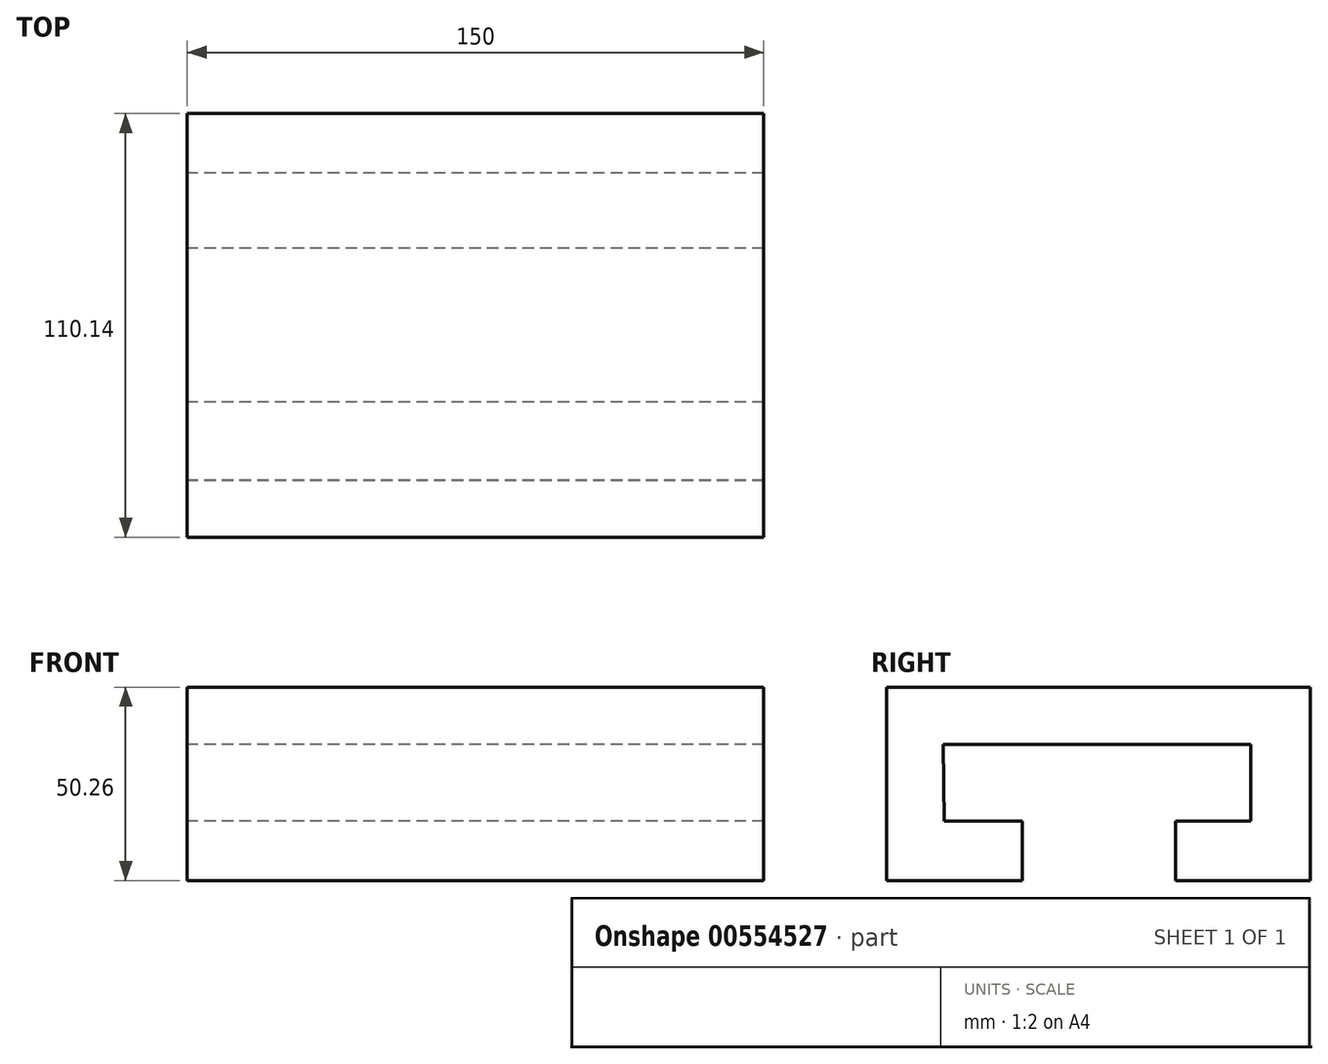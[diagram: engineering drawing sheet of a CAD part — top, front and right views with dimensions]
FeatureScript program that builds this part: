
annotation { "Feature Type Name" : "Feature", "Feature Type Description" : "" }
export const myFeature = defineFeature(function(context is Context, id is Id, definition is map)
    precondition{}
    {
        {
            var Q0;
            Q0=qCreatedBy(makeId("Right.planeOp"),FACE);
            var sketch = newSketch(context, id + "F0", { "sketchPlane" : qUnion([Q0])});
            skLineSegment(sketch, "E0", {"start": v(-41.19, 0) * mm, "end": v(38.81, 0) * mm});
            skLineSegment(sketch, "E1", {"start": v(38.81, 0) * mm, "end": v(38.81, -19.96) * mm});
            skLineSegment(sketch, "E2", {"start": v(38.81, -19.96) * mm, "end": v(19.23, -19.96) * mm});
            skLineSegment(sketch, "E3", {"start": v(19.23, -19.96) * mm, "end": v(19.23, -35.38) * mm});
            skLineSegment(sketch, "E4", {"start": v(19.23, -35.38) * mm, "end": v(54.25, -35.38) * mm});
            skLineSegment(sketch, "E5", {"start": v(54.25, -35.38) * mm, "end": v(54.25, 14.88) * mm});
            skLineSegment(sketch, "E6", {"start": v(54.25, 14.88) * mm, "end": v(-55.89, 14.88) * mm});
            skLineSegment(sketch, "E7", {"start": v(-55.89, 14.88) * mm, "end": v(-55.89, -35.38) * mm});
            skLineSegment(sketch, "E8", {"start": v(-55.89, -35.38) * mm, "end": v(-20.69, -35.38) * mm});
            skLineSegment(sketch, "E9", {"start": v(-20.69, -35.38) * mm, "end": v(-20.69, -19.96) * mm});
            skLineSegment(sketch, "E10", {"start": v(-20.69, -19.96) * mm, "end": v(-41, -19.96) * mm});
            skLineSegment(sketch, "E11", {"start": v(-41, -19.96) * mm, "end": v(-41.19, 0) * mm});
            skSolve(sketch);
        }
        {
            var Q0;
            Q0=makeQuery(id+"F0.imprint","IMPRINT",FACE,{"disambiguationData":[TD([[makeQuery(id+"F0.imprint","IMPRINT",EDGE,{"derivedFrom":sQuery(id+"F0.wireOp",EDGE,"E0")}),1.0]])]});
            extrude(context, id + "F1", {"entities" : qUnion([Q0]), "depth" : 150 * mm, "offsetDistance" : 25 * mm});
        }
    });
